# Revit family: RN 84230 Optiflex-Flowpress-Übergang
name_source: partatom
category: Rohrformteile
units: mm (PartAtom-declared; Revit-internal decimal feet)

## family parameters
Arbeitsebenenbasiert = Nein
Beim Laden mit Abzugskörper schneiden = Nein
Bemaßung runder Anschluss = Durchmesser verwenden
Gemeinsam genutzt = Nein
Immer vertikal = Ja
Teiletyp = Verbindung

## types (10) — shared parameters
1.010.00.2 Blattnummer der Richtlinie = 29
1.010.00.3 Ausgabedatum (Monat) der Richtlinie = 201308
1.010.00.4 Herstellername = R. Nussbaum AG
1.010.00.5 Revisionsdatum der Datei = 20190521
1.010.00.6 Webadresse des Herstellers = http://www.nussbaum.ch
1.100.00.4 Produktbezeichnung = Versorgung
1.110.00.2 Index = 5
1.110.00.4 Produktbezeichnung = Optiflex
1.960/3L.00.8 Link (URL) = https://www.nussbaum.ch
29.700.00.4 Produktname = Optiflex-Flowpress-Übergang, mit Aussengewinde
29.700.00.5 Produktkennung = 2
29.700.00.6 Querschnittsform = 1
29.700.00.7 Nennweitensystem = DN
29.700.00.8 Nenndrucksystem = PN
29.710.02.4 Nenndruck = 10
29.710.02.5 max. zul. Überdruck [hPa] = 1000
29.710.02.7 max. zul. Dauer-Betriebsdruck [hPa] = 1000
29.710.02.9 max. zul. Dauer-Betriebstemperatur [°C] = 70
Connector Visibility = Nein
EnclosingSpace Visibility = Nein
Hersteller = R. Nussbaum AG
URL = https://www.nussbaum.ch

## per-type parameters (varying)
- DN=50: 1.800.00.3 TGA-Nummer=01900500000000000000000000000000000000000000000016000000000000000010; 1.800.00.4 Kommentarfeld=84230.30, Optiflex-Flowpress-Übergang, mit Aussengewinde, DN=50, L=86, R=2; 1.810.00.3 Hersteller-Bestellnummer=84230.30; 1.810.00.4 DATANORM-Nummer=84230.30; 1.810.00.6 GTIN-Nummer=7612945744784; 29.710.02.10 Formstück-Gewicht [kg]=0.567; 29.710.02.3 Benennung=Optiflex-Flowpress-Übergang, mit Aussengewinde, DN=50, L=86, R=2; CONNECTOR0_DIAMETER_dX_0r=50 mm; CONNECTOR0_dX_01=28 mm; CONNECTOR0_ref_dX=28 mm; CONNECTOR1_DIAMETER_dX_0r=50 mm; CONNECTOR1_dX_00=63 mm; CONNECTOR1_dX_01=87 mm; CONNECTOR1_ref_dX=63 mm; Modell=84230.30; R. Nussbaum AG 84230.21 de Visibility=Nein; R. Nussbaum AG 84230.22 de Visibility=Nein; R. Nussbaum AG 84230.23 de Visibility=Nein; R. Nussbaum AG 84230.24 de Visibility=Nein; R. Nussbaum AG 84230.25 de Visibility=Nein; R. Nussbaum AG 84230.26 de Visibility=Nein; R. Nussbaum AG 84230.27 de Visibility=Nein; R. Nussbaum AG 84230.28 de Visibility=Nein; R. Nussbaum AG 84230.29 de Visibility=Nein; R. Nussbaum AG 84230.30 de Visibility=Ja; Typenkommentare=Optiflex-Flowpress-Übergang DN=50
- DN=40: 1.800.00.3 TGA-Nummer=01900500000000000000000000000000000000000000000016000000000000000009; 1.800.00.4 Kommentarfeld=84230.29, Optiflex-Flowpress-Übergang, mit Aussengewinde, DN=40, L=78, R=1½; 1.810.00.3 Hersteller-Bestellnummer=84230.29; 1.810.00.4 DATANORM-Nummer=84230.29; 1.810.00.6 GTIN-Nummer=7612945744623; 29.710.02.10 Formstück-Gewicht [kg]=0.418; 29.710.02.3 Benennung=Optiflex-Flowpress-Übergang, mit Aussengewinde, DN=40, L=78, R=1½; CONNECTOR0_DIAMETER_dX_0r=40 mm; CONNECTOR0_dX_01=26 mm; CONNECTOR0_ref_dX=26 mm; CONNECTOR1_DIAMETER_dX_0r=40 mm; CONNECTOR1_dX_00=60 mm; CONNECTOR1_dX_01=79 mm; CONNECTOR1_ref_dX=60 mm; Modell=84230.29; R. Nussbaum AG 84230.21 de Visibility=Nein; R. Nussbaum AG 84230.22 de Visibility=Nein; R. Nussbaum AG 84230.23 de Visibility=Nein; R. Nussbaum AG 84230.24 de Visibility=Nein; R. Nussbaum AG 84230.25 de Visibility=Nein; R. Nussbaum AG 84230.26 de Visibility=Nein; R. Nussbaum AG 84230.27 de Visibility=Nein; R. Nussbaum AG 84230.28 de Visibility=Nein; R. Nussbaum AG 84230.29 de Visibility=Ja; R. Nussbaum AG 84230.30 de Visibility=Nein; Typenkommentare=Optiflex-Flowpress-Übergang DN=40
- DN=32: 1.800.00.3 TGA-Nummer=01900500000000000000000000000000000000000000000016000000000000000008; 1.800.00.4 Kommentarfeld=84230.28, Optiflex-Flowpress-Übergang, mit Aussengewinde, DN=32, L=78, R=1¼; 1.810.00.3 Hersteller-Bestellnummer=84230.28; 1.810.00.4 DATANORM-Nummer=84230.28; 1.810.00.5 StLB-Nummer=346.245; 1.810.00.6 GTIN-Nummer=7612945730572; 29.710.02.10 Formstück-Gewicht [kg]=0.297; 29.710.02.3 Benennung=Optiflex-Flowpress-Übergang, mit Aussengewinde, DN=32, L=78, R=1¼; CONNECTOR0_DIAMETER_dX_0r=32 mm; CONNECTOR0_dX_01=26 mm; CONNECTOR0_ref_dX=26 mm; CONNECTOR1_DIAMETER_dX_0r=32 mm; CONNECTOR1_dX_00=59 mm; CONNECTOR1_dX_01=78 mm; CONNECTOR1_ref_dX=59 mm; Modell=84230.28; R. Nussbaum AG 84230.21 de Visibility=Nein; R. Nussbaum AG 84230.22 de Visibility=Nein; R. Nussbaum AG 84230.23 de Visibility=Nein; R. Nussbaum AG 84230.24 de Visibility=Nein; R. Nussbaum AG 84230.25 de Visibility=Nein; R. Nussbaum AG 84230.26 de Visibility=Nein; R. Nussbaum AG 84230.27 de Visibility=Nein; R. Nussbaum AG 84230.28 de Visibility=Ja; R. Nussbaum AG 84230.29 de Visibility=Nein; R. Nussbaum AG 84230.30 de Visibility=Nein; Typenkommentare=Optiflex-Flowpress-Übergang DN=32
- DN=25x25: 1.800.00.3 TGA-Nummer=01900500000000000000000000000000000000000000000016000000000000000007; 1.800.00.4 Kommentarfeld=84230.27, Optiflex-Flowpress-Übergang, mit Aussengewinde, DN=25x25, L=61, R=1; 1.810.00.3 Hersteller-Bestellnummer=84230.27; 1.810.00.4 DATANORM-Nummer=84230.27; 1.810.00.5 StLB-Nummer=346.234; 1.810.00.6 GTIN-Nummer=7612945730565; 29.710.02.10 Formstück-Gewicht [kg]=0.161; 29.710.02.3 Benennung=Optiflex-Flowpress-Übergang, mit Aussengewinde, DN=25x25, L=61, R=1; CONNECTOR0_DIAMETER_dX_0r=25 mm  [stored 0.082021 ft]; CONNECTOR0_dX_01=20 mm; CONNECTOR0_ref_dX=20 mm; CONNECTOR1_DIAMETER_dX_0r=25 mm  [stored 0.082021 ft]; CONNECTOR1_dX_00=44 mm; CONNECTOR1_dX_01=61 mm; CONNECTOR1_ref_dX=44 mm; Modell=84230.27; R. Nussbaum AG 84230.21 de Visibility=Nein; R. Nussbaum AG 84230.22 de Visibility=Nein; R. Nussbaum AG 84230.23 de Visibility=Nein; R. Nussbaum AG 84230.24 de Visibility=Nein; R. Nussbaum AG 84230.25 de Visibility=Nein; R. Nussbaum AG 84230.26 de Visibility=Nein; R. Nussbaum AG 84230.27 de Visibility=Ja; R. Nussbaum AG 84230.28 de Visibility=Nein; R. Nussbaum AG 84230.29 de Visibility=Nein; R. Nussbaum AG 84230.30 de Visibility=Nein; Typenkommentare=Optiflex-Flowpress-Übergang DN=25x25
- DN=25x20: 1.800.00.3 TGA-Nummer=01900500000000000000000000000000000000000000000016000000000000000006; 1.800.00.4 Kommentarfeld=84230.26, Optiflex-Flowpress-Übergang, mit Aussengewinde, DN=25x20, L=61, R=1; 1.810.00.3 Hersteller-Bestellnummer=84230.26; 1.810.00.4 DATANORM-Nummer=84230.26; 1.810.00.5 StLB-Nummer=346.233; 1.810.00.6 GTIN-Nummer=7612945730558; 29.710.02.10 Formstück-Gewicht [kg]=0.137; 29.710.02.3 Benennung=Optiflex-Flowpress-Übergang, mit Aussengewinde, DN=25x20, L=61, R=1; CONNECTOR0_DIAMETER_dX_0r=20 mm; CONNECTOR0_dX_01=20 mm; CONNECTOR0_ref_dX=20 mm; CONNECTOR1_DIAMETER_dX_0r=25 mm  [stored 0.082021 ft]; CONNECTOR1_dX_00=44 mm; CONNECTOR1_dX_01=61 mm; CONNECTOR1_ref_dX=44 mm; Modell=84230.26; R. Nussbaum AG 84230.21 de Visibility=Nein; R. Nussbaum AG 84230.22 de Visibility=Nein; R. Nussbaum AG 84230.23 de Visibility=Nein; R. Nussbaum AG 84230.24 de Visibility=Nein; R. Nussbaum AG 84230.25 de Visibility=Nein; R. Nussbaum AG 84230.26 de Visibility=Ja; R. Nussbaum AG 84230.27 de Visibility=Nein; R. Nussbaum AG 84230.28 de Visibility=Nein; R. Nussbaum AG 84230.29 de Visibility=Nein; R. Nussbaum AG 84230.30 de Visibility=Nein; Typenkommentare=Optiflex-Flowpress-Übergang DN=25x20
- DN=20: 1.800.00.3 TGA-Nummer=01900500000000000000000000000000000000000000000016000000000000000005; 1.800.00.4 Kommentarfeld=84230.25, Optiflex-Flowpress-Übergang, mit Aussengewinde, DN=20, L=55, R=¾; 1.810.00.3 Hersteller-Bestellnummer=84230.25; 1.810.00.4 DATANORM-Nummer=84230.25; 1.810.00.5 StLB-Nummer=346.223; 1.810.00.6 GTIN-Nummer=7612945730541; 29.710.02.10 Formstück-Gewicht [kg]=0.098; 29.710.02.3 Benennung=Optiflex-Flowpress-Übergang, mit Aussengewinde, DN=20, L=55, R=¾; CONNECTOR0_DIAMETER_dX_0r=20 mm; CONNECTOR0_dX_01=20 mm; CONNECTOR0_ref_dX=20 mm; CONNECTOR1_DIAMETER_dX_0r=20 mm; CONNECTOR1_dX_00=40 mm; CONNECTOR1_dX_01=55 mm; CONNECTOR1_ref_dX=40 mm; Modell=84230.25; R. Nussbaum AG 84230.21 de Visibility=Nein; R. Nussbaum AG 84230.22 de Visibility=Nein; R. Nussbaum AG 84230.23 de Visibility=Nein; R. Nussbaum AG 84230.24 de Visibility=Nein; R. Nussbaum AG 84230.25 de Visibility=Ja; R. Nussbaum AG 84230.26 de Visibility=Nein; R. Nussbaum AG 84230.27 de Visibility=Nein; R. Nussbaum AG 84230.28 de Visibility=Nein; R. Nussbaum AG 84230.29 de Visibility=Nein; R. Nussbaum AG 84230.30 de Visibility=Nein; Typenkommentare=Optiflex-Flowpress-Übergang DN=20
- DN=20x15: 1.800.00.3 TGA-Nummer=01900500000000000000000000000000000000000000000016000000000000000004; 1.800.00.4 Kommentarfeld=84230.24, Optiflex-Flowpress-Übergang, mit Aussengewinde, DN=20x15, L=48, R=¾; 1.810.00.3 Hersteller-Bestellnummer=84230.24; 1.810.00.4 DATANORM-Nummer=84230.24; 1.810.00.5 StLB-Nummer=346.222; 1.810.00.6 GTIN-Nummer=7612945730534; 29.710.02.10 Formstück-Gewicht [kg]=0.071; 29.710.02.3 Benennung=Optiflex-Flowpress-Übergang, mit Aussengewinde, DN=20x15, L=48, R=¾; CONNECTOR0_DIAMETER_dX_0r=15 mm; CONNECTOR0_dX_01=14 mm  [stored 0.0459318 ft]; CONNECTOR0_ref_dX=14 mm  [stored 0.0459318 ft]; CONNECTOR1_DIAMETER_dX_0r=20 mm; CONNECTOR1_dX_00=33 mm; CONNECTOR1_dX_01=48 mm; CONNECTOR1_ref_dX=33 mm; Modell=84230.24; R. Nussbaum AG 84230.21 de Visibility=Nein; R. Nussbaum AG 84230.22 de Visibility=Nein; R. Nussbaum AG 84230.23 de Visibility=Nein; R. Nussbaum AG 84230.24 de Visibility=Ja; R. Nussbaum AG 84230.25 de Visibility=Nein; R. Nussbaum AG 84230.26 de Visibility=Nein; R. Nussbaum AG 84230.27 de Visibility=Nein; R. Nussbaum AG 84230.28 de Visibility=Nein; R. Nussbaum AG 84230.29 de Visibility=Nein; R. Nussbaum AG 84230.30 de Visibility=Nein; Typenkommentare=Optiflex-Flowpress-Übergang DN=20x15
- DN=20x1: 1.800.00.3 TGA-Nummer=01900500000000000000000000000000000000000000000016000000000000000003; 1.800.00.4 Kommentarfeld=84230.23, Optiflex-Flowpress-Übergang, mit Aussengewinde, DN=20x15, L=48, R=¾; 1.810.00.3 Hersteller-Bestellnummer=84230.23; 1.810.00.4 DATANORM-Nummer=84230.23; 1.810.00.5 StLB-Nummer=346.221; 1.810.00.6 GTIN-Nummer=7612945730527; 29.710.02.10 Formstück-Gewicht [kg]=0.065; 29.710.02.3 Benennung=Optiflex-Flowpress-Übergang, mit Aussengewinde, DN=20x15, L=48, R=¾; CONNECTOR0_DIAMETER_dX_0r=12 mm  [stored 0.0393701 ft]; CONNECTOR0_dX_01=14 mm  [stored 0.0459318 ft]; CONNECTOR0_ref_dX=14 mm  [stored 0.0459318 ft]; CONNECTOR1_DIAMETER_dX_0r=20 mm; CONNECTOR1_dX_00=33 mm; CONNECTOR1_dX_01=48 mm; CONNECTOR1_ref_dX=33 mm; Modell=84230.23; R. Nussbaum AG 84230.21 de Visibility=Nein; R. Nussbaum AG 84230.22 de Visibility=Nein; R. Nussbaum AG 84230.23 de Visibility=Ja; R. Nussbaum AG 84230.24 de Visibility=Nein; R. Nussbaum AG 84230.25 de Visibility=Nein; R. Nussbaum AG 84230.26 de Visibility=Nein; R. Nussbaum AG 84230.27 de Visibility=Nein; R. Nussbaum AG 84230.28 de Visibility=Nein; R. Nussbaum AG 84230.29 de Visibility=Nein; R. Nussbaum AG 84230.30 de Visibility=Nein; Typenkommentare=Optiflex-Flowpress-Übergang DN=20x15
- DN=15: 1.800.00.3 TGA-Nummer=01900500000000000000000000000000000000000000000016000000000000000002; 1.800.00.4 Kommentarfeld=84230.22, Optiflex-Flowpress-Übergang, mit Aussengewinde, DN=15, L=49, R=½; 1.810.00.3 Hersteller-Bestellnummer=84230.22; 1.810.00.4 DATANORM-Nummer=84230.22; 1.810.00.5 StLB-Nummer=346.212; 1.810.00.6 GTIN-Nummer=7612945730510; 29.710.02.10 Formstück-Gewicht [kg]=0.058; 29.710.02.3 Benennung=Optiflex-Flowpress-Übergang, mit Aussengewinde, DN=15, L=49, R=½; CONNECTOR0_DIAMETER_dX_0r=15 mm; CONNECTOR0_dX_01=14 mm  [stored 0.0459318 ft]; CONNECTOR0_ref_dX=14 mm  [stored 0.0459318 ft]; CONNECTOR1_DIAMETER_dX_0r=15 mm; CONNECTOR1_dX_00=36 mm; CONNECTOR1_dX_01=49 mm; CONNECTOR1_ref_dX=36 mm; Modell=84230.22; R. Nussbaum AG 84230.21 de Visibility=Nein; R. Nussbaum AG 84230.22 de Visibility=Ja; R. Nussbaum AG 84230.23 de Visibility=Nein; R. Nussbaum AG 84230.24 de Visibility=Nein; R. Nussbaum AG 84230.25 de Visibility=Nein; R. Nussbaum AG 84230.26 de Visibility=Nein; R. Nussbaum AG 84230.27 de Visibility=Nein; R. Nussbaum AG 84230.28 de Visibility=Nein; R. Nussbaum AG 84230.29 de Visibility=Nein; R. Nussbaum AG 84230.30 de Visibility=Nein; Typenkommentare=Optiflex-Flowpress-Übergang DN=15
- DN=15x12: 1.800.00.3 TGA-Nummer=01900500000000000000000000000000000000000000000016000000000000000001; 1.800.00.4 Kommentarfeld=84230.21, Optiflex-Flowpress-Übergang, mit Aussengewinde, DN=15x12, L=47, R=½; 1.810.00.3 Hersteller-Bestellnummer=84230.21; 1.810.00.4 DATANORM-Nummer=84230.21; 1.810.00.5 StLB-Nummer=346.211; 1.810.00.6 GTIN-Nummer=7612945730503; 29.710.02.10 Formstück-Gewicht [kg]=0.05; 29.710.02.3 Benennung=Optiflex-Flowpress-Übergang, mit Aussengewinde, DN=15x12, L=47, R=½; CONNECTOR0_DIAMETER_dX_0r=12 mm  [stored 0.0393701 ft]; CONNECTOR0_dX_01=14 mm  [stored 0.0459318 ft]; CONNECTOR0_ref_dX=14 mm  [stored 0.0459318 ft]; CONNECTOR1_DIAMETER_dX_0r=15 mm; CONNECTOR1_dX_00=34 mm; CONNECTOR1_dX_01=47 mm; CONNECTOR1_ref_dX=34 mm; Modell=84230.21; R. Nussbaum AG 84230.21 de Visibility=Ja; R. Nussbaum AG 84230.22 de Visibility=Nein; R. Nussbaum AG 84230.23 de Visibility=Nein; R. Nussbaum AG 84230.24 de Visibility=Nein; R. Nussbaum AG 84230.25 de Visibility=Nein; R. Nussbaum AG 84230.26 de Visibility=Nein; R. Nussbaum AG 84230.27 de Visibility=Nein; R. Nussbaum AG 84230.28 de Visibility=Nein; R. Nussbaum AG 84230.29 de Visibility=Nein; R. Nussbaum AG 84230.30 de Visibility=Nein; Typenkommentare=Optiflex-Flowpress-Übergang DN=15x12

note: [stored X ft] marks values corroborated as IEEE doubles in the binary element streams (Revit-internal decimal feet)

## geometry (parser evidence)
native form markers: Sweep x1
no freeform markers — native parametric forms only
